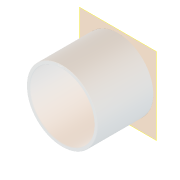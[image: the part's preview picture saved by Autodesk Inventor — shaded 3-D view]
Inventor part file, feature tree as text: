
AUTODESK INVENTOR PART (.ipt)
format: ipt  version: 2021 (Build 250183000, 183)  size: 579,584 bytes
history: native  units: in
note: dims shown in document units (in); Inventor stores cm internally (conversion verified against a paired STEP export)
features: plane x1, split x1, other x1
ambient origin geometry x8: Origin, YZ Plane, XZ Plane, XY Plane, X Axis, Y Axis, Z Axis, Center Point
bodies: Solid1 (feature_tree)
feature tree (3):
  plane  "Work Plane1"
  split  "Split1"
  other  "TTN122478-1-solid1"
